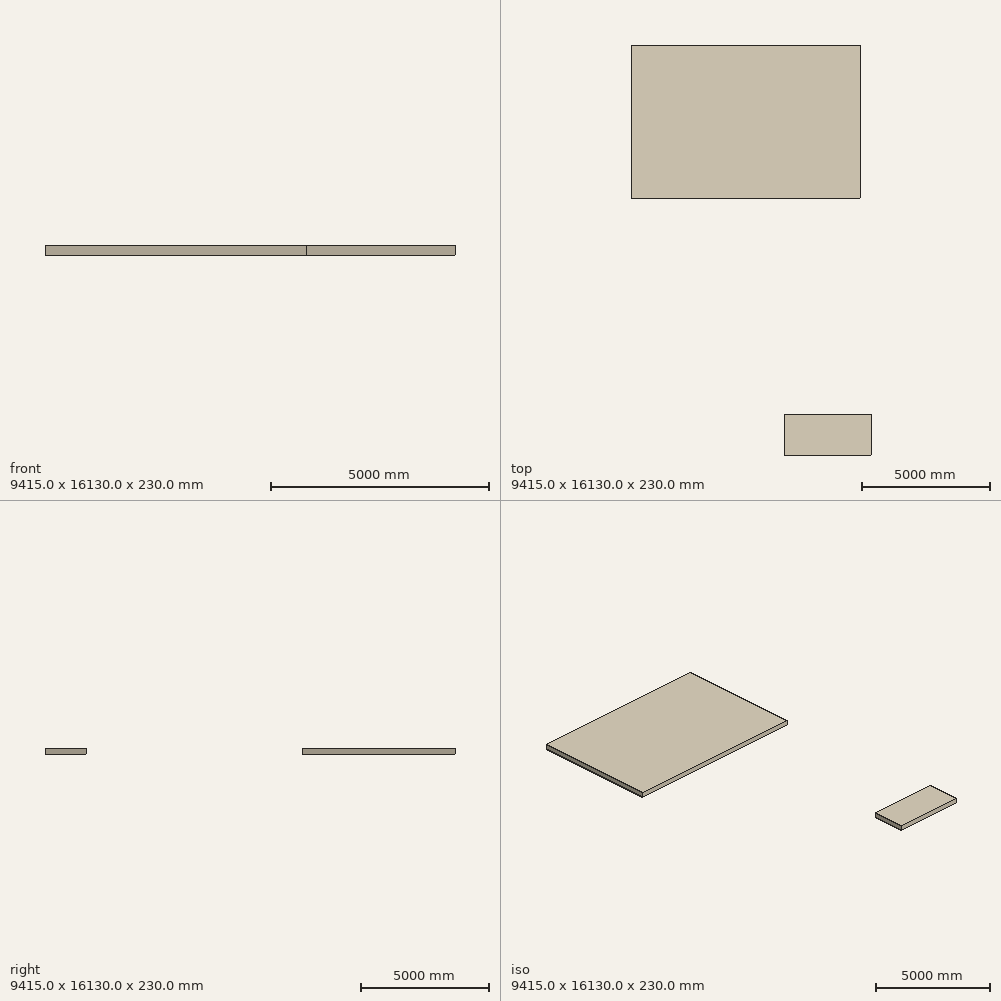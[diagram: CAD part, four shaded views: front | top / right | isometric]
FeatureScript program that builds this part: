
annotation { "Feature Type Name" : "Feature", "Feature Type Description" : "" }
export const myFeature = defineFeature(function(context is Context, id is Id, definition is map)
    precondition{}
    {
        {
            var Q0;
            Q0=qCreatedBy(makeId("Top.planeOp"),FACE);
            var sketch = newSketch(context, id + "F0", { "sketchPlane" : qUnion([Q0])});
            skLineSegment(sketch, "E0.bottom", {"start": v(-5905.26, 9582.96) * mm, "end": v(3094.74, 9582.96) * mm});
            skLineSegment(sketch, "E0.top", {"start": v(-4005.26, -4917.04) * mm, "end": v(5674.74, -4917.04) * mm});
            skLineSegment(sketch, "E0.left", {"start": v(-5905.26, 9582.96) * mm, "end": v(-5905.26, 882.96) * mm});
            skLineSegment(sketch, "E1.top", {"start": v(5674.74, 3582.96) * mm, "end": v(3094.74, 3582.96) * mm});
            skLineSegment(sketch, "E1.right", {"start": v(3094.74, 9582.96) * mm, "end": v(3094.74, 3582.96) * mm});
            skLineSegment(sketch, "E2.top", {"start": v(-5905.26, 882.96) * mm, "end": v(-4005.26, 882.96) * mm});
            skLineSegment(sketch, "E3", {"start": v(3094.74, 3582.96) * mm, "end": v(-5905.26, 3582.96) * mm});
            skLineSegment(sketch, "E4.0", {"start": v(-4005.26, -4917.04) * mm, "end": v(-4005.26, 882.96) * mm});
            skLineSegment(sketch, "E5.0", {"start": v(99.74, -4917.04) * mm, "end": v(99.74, -6547.04) * mm});
            skLineSegment(sketch, "E6.0", {"start": v(3509.74, -6547.04) * mm, "end": v(3509.74, -4917.04) * mm});
            skLineSegment(sketch, "E7.0", {"start": v(99.74, -6547.04) * mm, "end": v(3509.74, -6547.04) * mm});
            skLineSegment(sketch, "E8.0", {"start": v(5674.74, 3582.96) * mm, "end": v(5674.74, -4917.04) * mm});
            skLineSegment(sketch, "E9.0", {"start": v(-1705.26, -607.04) * mm, "end": v(-1705.26, -2167.04) * mm});
            skLineSegment(sketch, "E10.0", {"start": v(-1705.26, -2167.04) * mm, "end": v(-3095.26, -2167.04) * mm});
            skLineSegment(sketch, "E11.0", {"start": v(-1705.26, -607.04) * mm, "end": v(-2685.26, -607.04) * mm});
            skLineSegment(sketch, "E12.0", {"start": v(-2685.26, -1137.04) * mm, "end": v(-3095.26, -1137.04) * mm});
            skLineSegment(sketch, "E13.trimOffspring", {"start": v(-2685.26, -607.04) * mm, "end": v(-2685.26, -1137.04) * mm});
            skLineSegment(sketch, "E14.trimOffspring", {"start": v(-3095.26, -1137.04) * mm, "end": v(-3095.26, -2167.04) * mm});
            skSolve(sketch);
        }
        {
            var Q0;
            {var subQ0=sQuery(id+"F0.wireOp",EDGE,"E0.bottom");Q0=makeQuery(id+"F0.imprint","IMPRINT",FACE,{"disambiguationData":[TD([[makeQuery(id+"F0.imprint","IMPRINT",EDGE,{"derivedFrom":subQ0}),-1.0]])]});}
            var Q1;
            Q1=makeQuery(id+"F0.imprint","IMPRINT",FACE,{"disambiguationData":[TD([[makeQuery(id+"F0.imprint","IMPRINT",EDGE,{"derivedFrom":sQuery(id+"F0.wireOp",EDGE,"E1.top")}),1.0]])]});
            var Q2;
            {var subQ0=sQuery(id+"F0.wireOp",EDGE,"E5.0");Q2=makeQuery(id+"F0.imprint","IMPRINT",FACE,{"disambiguationData":[TD([[makeQuery(id+"F0.imprint","IMPRINT",EDGE,{"derivedFrom":subQ0}),1.0]])]});}
            extrude(context, id + "F1", {"entities" : qUnion([Q0, Q1, Q2]), "depth" : 230 * mm});
        }
    });
